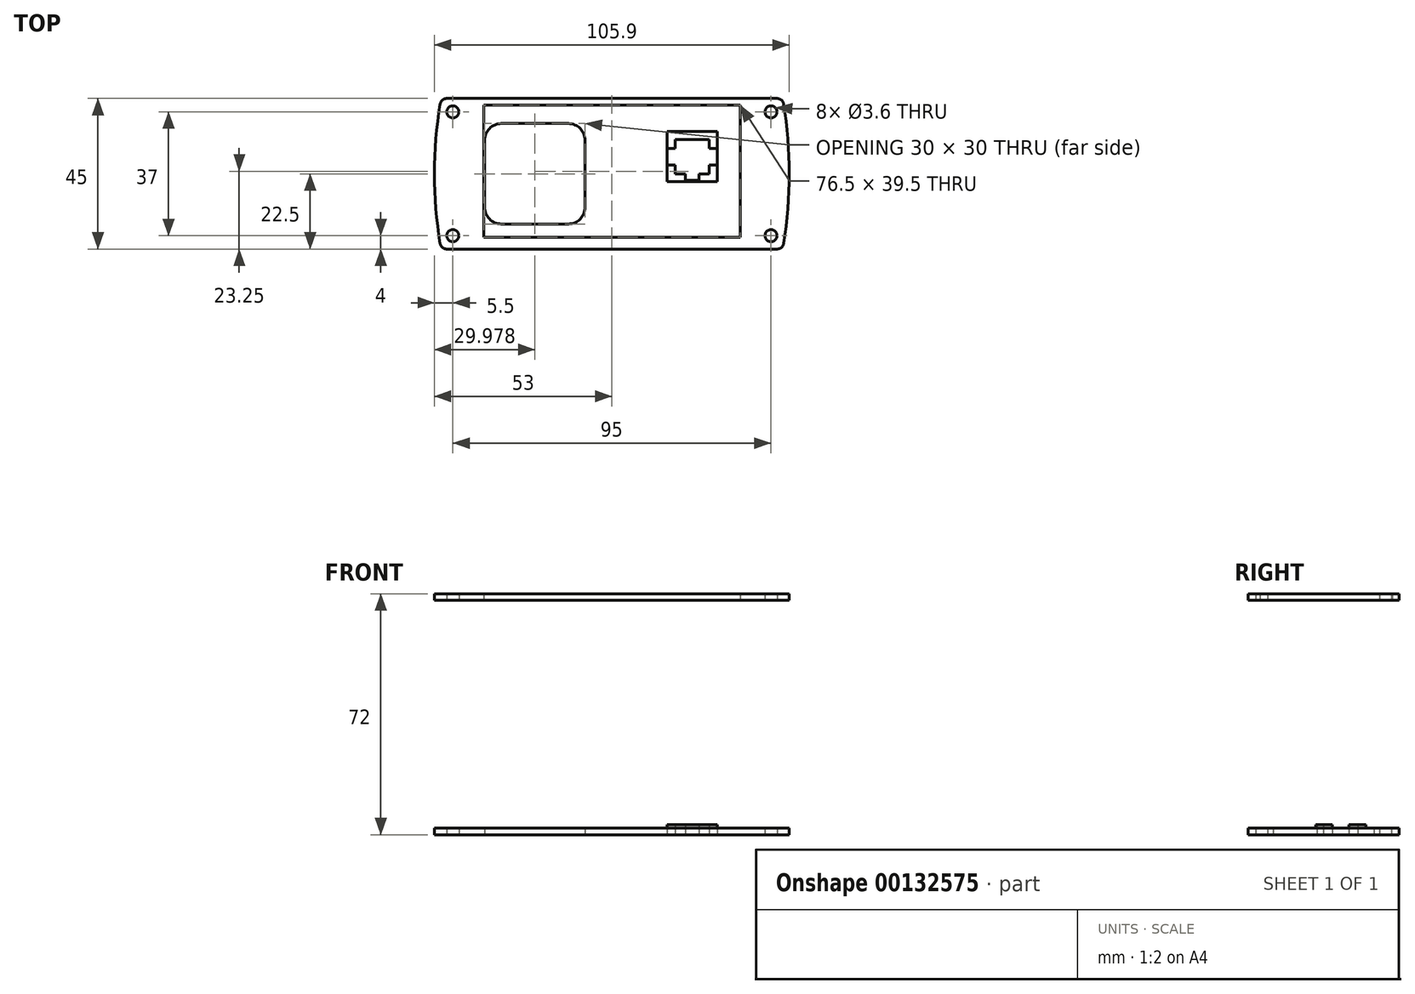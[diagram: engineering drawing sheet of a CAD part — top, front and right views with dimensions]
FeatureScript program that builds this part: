
annotation { "Feature Type Name" : "Feature", "Feature Type Description" : "" }
export const myFeature = defineFeature(function(context is Context, id is Id, definition is map)
    precondition{}
    {
        {
            var Q0;
            Q0=qCreatedBy(makeId("Top.planeOp"),FACE);
            var sketch = newSketch(context, id + "F0", { "sketchPlane" : qUnion([Q0])});
            skLineSegment(sketch, "E0.bottom", {"start": v(-38.25, 20.5) * mm, "end": v(38.25, 20.5) * mm});
            skLineSegment(sketch, "E0.top", {"start": v(-38.25, -19) * mm, "end": v(38.25, -19) * mm});
            skLineSegment(sketch, "E0.left", {"start": v(-38.25, 20.5) * mm, "end": v(-38.25, -19) * mm});
            skLineSegment(sketch, "E0.right", {"start": v(38.25, 20.5) * mm, "end": v(38.25, -19) * mm});
            skLineSegment(sketch, "E1.left", {"start": v(-53, 22.5) * mm, "end": v(-53, -22.5) * mm, "construction": true});
            skLineSegment(sketch, "E1.right", {"start": v(53, 22.5) * mm, "end": v(53, -22.5) * mm, "construction": true});
            skLineSegment(sketch, "E2.0", {"start": v(-51, 22.5) * mm, "end": v(-51, -22.5) * mm, "construction": true});
            skLineSegment(sketch, "E3.0", {"start": v(51, 22.5) * mm, "end": v(51, -22.5) * mm, "construction": true});
            skArc(sketch, "E4", {"start": v(-51.29, 20.83) * mm, "mid": v(-53, 0) * mm, "end": v(-51.29, -20.83) * mm});
            skArc(sketch, "E5", {"start": v(51.28, -20.81) * mm, "mid": v(52.9, 0) * mm, "end": v(51.28, 20.81) * mm});
            skLineSegment(sketch, "E6", {"start": v(49.3, 22.5) * mm, "end": v(-49.32, 22.5) * mm});
            skLineSegment(sketch, "E7", {"start": v(-49.32, -22.5) * mm, "end": v(49.3, -22.5) * mm});
            skPoint(sketch, "E8.visualSharp", {"position": v(-51, -22.5) * mm});
            skArc(sketch, "E8.filletArc", {"start": v(-51.29, -20.83) * mm, "mid": v(-50.6, -22.03) * mm, "end": v(-49.32, -22.5) * mm});
            skPoint(sketch, "E9.visualSharp", {"position": v(51, -22.5) * mm});
            skArc(sketch, "E9.filletArc", {"start": v(49.3, -22.5) * mm, "mid": v(50.6, -22.02) * mm, "end": v(51.28, -20.81) * mm});
            skPoint(sketch, "E10.visualSharp", {"position": v(-51, 22.5) * mm});
            skArc(sketch, "E10.filletArc", {"start": v(-49.32, 22.5) * mm, "mid": v(-50.6, 22.03) * mm, "end": v(-51.29, 20.83) * mm});
            skPoint(sketch, "E11.visualSharp", {"position": v(51, 22.5) * mm});
            skArc(sketch, "E11.filletArc", {"start": v(51.28, 20.81) * mm, "mid": v(50.6, 22.02) * mm, "end": v(49.3, 22.5) * mm});
            skCircle(sketch, "E12", {"center": v(-47.5, 18.5) * mm, "radius": 1.8 * mm});
            skCircle(sketch, "E13.0.1.0", {"center": v(-47.5, -18.5) * mm, "radius": 1.8 * mm});
            skCircle(sketch, "E13.1.0.0", {"center": v(47.5, 18.5) * mm, "radius": 1.8 * mm});
            skCircle(sketch, "E13.1.1.0", {"center": v(47.5, -18.5) * mm, "radius": 1.8 * mm});
            skLineSegment(sketch, "E13.direction1", {"start": v(-47.5, 18.5) * mm, "end": v(47.5, 18.5) * mm, "construction": true});
            skLineSegment(sketch, "E13.direction2", {"start": v(-47.5, 18.5) * mm, "end": v(-47.5, -18.5) * mm, "construction": true});
            skSolve(sketch);
        }
        {
            var Q0;
            Q0=makeQuery(id+"F0.imprint","IMPRINT",FACE,{"disambiguationData":[TD([[makeQuery(id+"F0.imprint","IMPRINT",EDGE,{"derivedFrom":sQuery(id+"F0.wireOp",EDGE,"E0.bottom")}),1.0]])]});
            extrude(context, id + "F1", {"entities" : qUnion([Q0]), "depth" : 2 * mm});
        }
        {
            var Q0;
            Q0=qCreatedBy(makeId("Top.planeOp"),FACE);
            cPlane(context, id + "F2", {"entities" : qUnion([Q0]), "cplaneType" : CPlaneType.OFFSET, "offset" : 70 * mm, "oppositeDirection" : true, "width" : 150 * mm, "height" : 150 * mm});
        }
        {
            var Q0;
            Q0=qCreatedBy(id+"F2.planeOp",FACE);
            var sketch = newSketch(context, id + "F3", { "sketchPlane" : qUnion([Q0])});
            skArc(sketch, "E14.0", {"start": v(-51.29, 20.83) * mm, "mid": v(-53, 0) * mm, "end": v(-51.29, -20.83) * mm});
            skLineSegment(sketch, "E14.1", {"start": v(-49.32, -22.5) * mm, "end": v(49.3, -22.5) * mm});
            skArc(sketch, "E14.2", {"start": v(-51.29, -20.83) * mm, "mid": v(-50.6, -22.03) * mm, "end": v(-49.32, -22.5) * mm});
            skCircle(sketch, "E14.3", {"center": v(-47.5, -18.5) * mm, "radius": 1.8 * mm});
            skLineSegment(sketch, "E14.7", {"start": v(49.3, 22.5) * mm, "end": v(-49.32, 22.5) * mm});
            skArc(sketch, "E14.8", {"start": v(-49.32, 22.5) * mm, "mid": v(-50.6, 22.03) * mm, "end": v(-51.29, 20.83) * mm});
            skCircle(sketch, "E14.9", {"center": v(-47.5, 18.5) * mm, "radius": 1.8 * mm});
            skCircle(sketch, "E14.10", {"center": v(47.5, 18.5) * mm, "radius": 1.8 * mm});
            skArc(sketch, "E14.12", {"start": v(51.28, -20.81) * mm, "mid": v(52.9, 0) * mm, "end": v(51.28, 20.81) * mm});
            skArc(sketch, "E14.13", {"start": v(51.28, 20.81) * mm, "mid": v(50.6, 22.02) * mm, "end": v(49.3, 22.5) * mm});
            skCircle(sketch, "E14.14", {"center": v(47.5, -18.5) * mm, "radius": 1.8 * mm});
            skArc(sketch, "E14.15", {"start": v(49.3, -22.5) * mm, "mid": v(50.6, -22.02) * mm, "end": v(51.28, -20.81) * mm});
            skPoint(sketch, "E14.16", {"position": v(-50.6, -22.03) * mm});
            skLineSegment(sketch, "E15.bottom", {"start": v(-33.02, -15) * mm, "end": v(-13.02, -15) * mm});
            skLineSegment(sketch, "E15.top", {"start": v(-33.02, 15) * mm, "end": v(-13.02, 15) * mm});
            skLineSegment(sketch, "E15.left", {"start": v(-38.02, -10) * mm, "end": v(-38.02, 10) * mm});
            skLineSegment(sketch, "E15.right", {"start": v(-8.02, -10) * mm, "end": v(-8.02, 10) * mm});
            skPoint(sketch, "E16.visualSharp", {"position": v(-8.02, -15) * mm});
            skArc(sketch, "E16.filletArc", {"start": v(-13.02, -15) * mm, "mid": v(-9.49, -13.54) * mm, "end": v(-8.02, -10) * mm});
            skPoint(sketch, "E17.visualSharp", {"position": v(-8.02, 15) * mm});
            skArc(sketch, "E17.filletArc", {"start": v(-8.02, 10) * mm, "mid": v(-9.49, 13.54) * mm, "end": v(-13.02, 15) * mm});
            skPoint(sketch, "E18.visualSharp", {"position": v(-38.02, 15) * mm});
            skArc(sketch, "E18.filletArc", {"start": v(-33.02, 15) * mm, "mid": v(-36.56, 13.54) * mm, "end": v(-38.02, 10) * mm});
            skPoint(sketch, "E19.visualSharp", {"position": v(-38.02, -15) * mm});
            skArc(sketch, "E19.filletArc", {"start": v(-38.02, -10) * mm, "mid": v(-36.56, -13.54) * mm, "end": v(-33.02, -15) * mm});
            skLineSegment(sketch, "E20.bottom", {"start": v(18.86, 0) * mm, "end": v(29.06, 0) * mm});
            skLineSegment(sketch, "E20.top", {"start": v(18.86, 10.2) * mm, "end": v(29.06, 10.2) * mm});
            skLineSegment(sketch, "E20.left", {"start": v(18.86, 0) * mm, "end": v(18.86, 10.2) * mm});
            skLineSegment(sketch, "E20.right", {"start": v(29.06, 0) * mm, "end": v(29.06, 10.2) * mm});
            skLineSegment(sketch, "E21.bottom", {"start": v(21.96, -2) * mm, "end": v(25.96, -2) * mm});
            skLineSegment(sketch, "E21.top", {"start": v(21.96, 2) * mm, "end": v(25.96, 2) * mm});
            skLineSegment(sketch, "E21.left", {"start": v(21.96, -2) * mm, "end": v(21.96, 2) * mm});
            skLineSegment(sketch, "E21.right", {"start": v(25.96, -2) * mm, "end": v(25.96, 2) * mm});
            skPoint(sketch, "E21.middle", {"position": v(23.96, 0) * mm});
            skLineSegment(sketch, "E22", {"start": v(18.86, 5.1) * mm, "end": v(29.06, 5.1) * mm, "construction": true});
            skLineSegment(sketch, "E23.bottom", {"start": v(16.46, 2.6) * mm, "end": v(31.46, 2.6) * mm});
            skLineSegment(sketch, "E23.top", {"start": v(16.46, 7.6) * mm, "end": v(31.46, 7.6) * mm});
            skLineSegment(sketch, "E23.left", {"start": v(16.46, 2.6) * mm, "end": v(16.46, 7.6) * mm});
            skLineSegment(sketch, "E23.right", {"start": v(31.46, 2.6) * mm, "end": v(31.46, 7.6) * mm});
            skPoint(sketch, "E23.middle", {"position": v(23.96, 5.1) * mm});
            skLineSegment(sketch, "E24.bottom", {"start": v(16.46, 12.6) * mm, "end": v(31.46, 12.6) * mm});
            skLineSegment(sketch, "E24.top", {"start": v(16.46, -2.4) * mm, "end": v(31.46, -2.4) * mm});
            skLineSegment(sketch, "E24.left", {"start": v(16.46, 12.6) * mm, "end": v(16.46, -2.4) * mm});
            skLineSegment(sketch, "E24.right", {"start": v(31.46, 12.6) * mm, "end": v(31.46, -2.4) * mm});
            skSolve(sketch);
        }
        {
            var Q0;
            Q0=makeQuery(id+"F3.imprint","IMPRINT",FACE,{"disambiguationData":[TD([[makeQuery(id+"F3.imprint","IMPRINT",EDGE,{"derivedFrom":sQuery(id+"F3.wireOp",EDGE,"E14.0")}),1.0]])]});
            extrude(context, id + "F4", {"entities" : qUnion([Q0]), "depth" : 2 * mm});
        }
        {
            var Q0;
            {var subQ1=sQuery(id+"F3.wireOp",EDGE,"E20.top");Q0=makeQuery(id+"F3.imprint","IMPRINT",FACE,{"disambiguationData":[TD([[makeQuery(id+"F3.imprint","IMPRINT",EDGE,{"derivedFrom":subQ1}),1.0]])]});}
            var Q1;
            {var subQ15=sQuery(id+"F3.wireOp",EDGE,"E21.bottom");Q1=makeQuery(id+"F3.imprint","IMPRINT",FACE,{"disambiguationData":[TD([[makeQuery(id+"F3.imprint","IMPRINT",EDGE,{"derivedFrom":subQ15}),-1.0]])]});}
            extrude(context, id + "F5", {"entities" : qUnion([Q0, Q1]), "operationType" : NewBodyOperationType.ADD, "depth" : 3 * mm});
        }
    });
